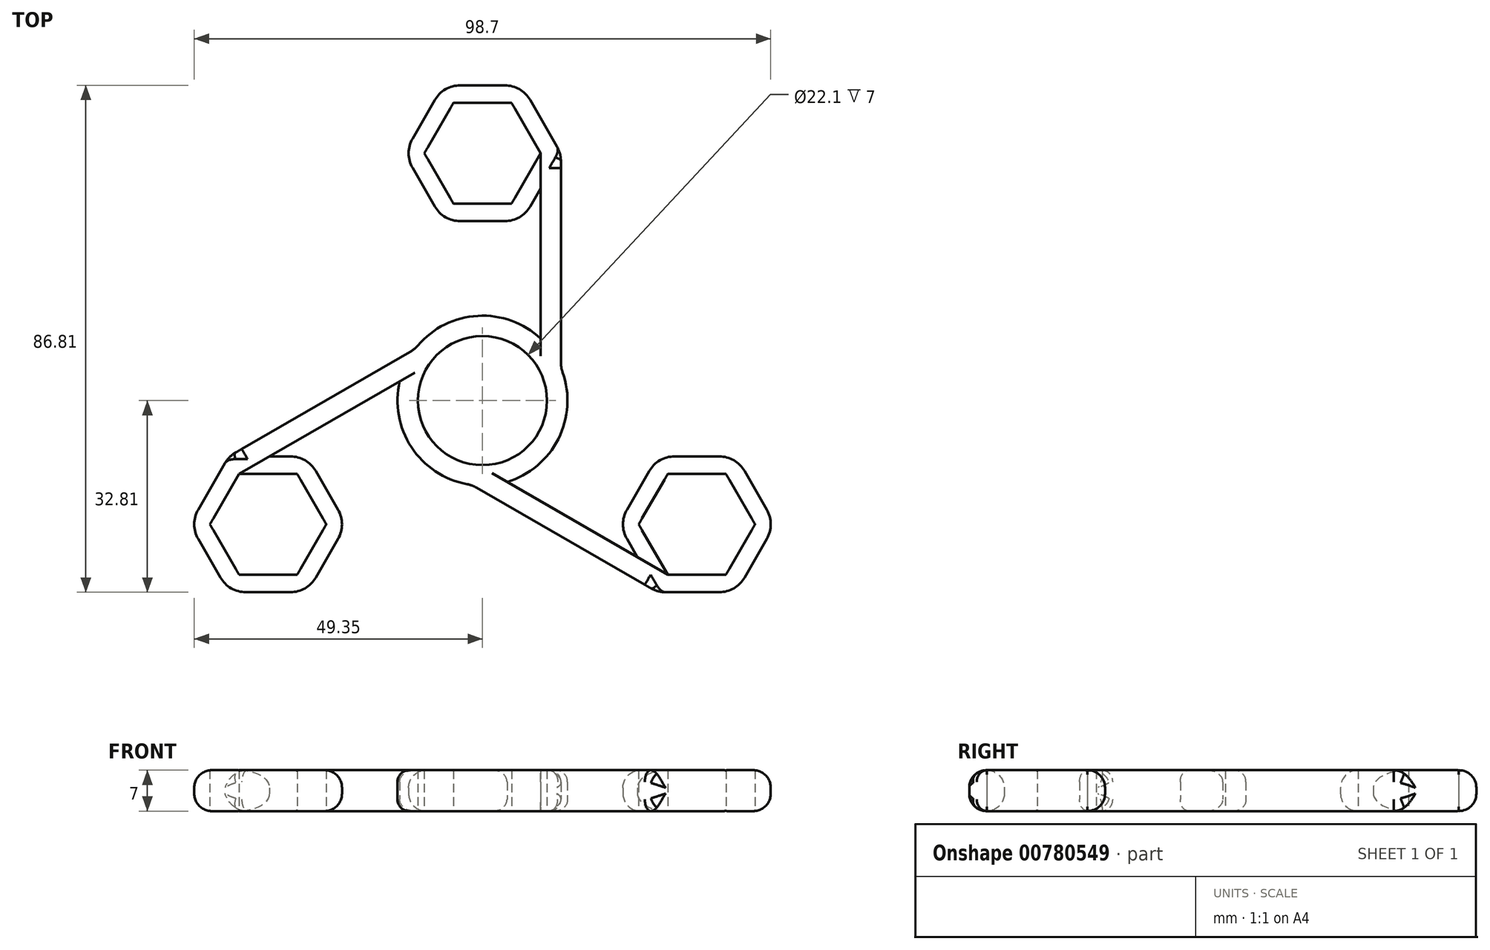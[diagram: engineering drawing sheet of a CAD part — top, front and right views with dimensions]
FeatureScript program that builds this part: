
annotation { "Feature Type Name" : "Feature", "Feature Type Description" : "" }
export const myFeature = defineFeature(function(context is Context, id is Id, definition is map)
    precondition{}
    {
        {
            var Q0;
            Q0=qCreatedBy(makeId("Top.planeOp"),FACE);
            var sketch = newSketch(context, id + "F0", { "sketchPlane" : qUnion([Q0])});
            skCircle(sketch, "E0", {"center": v(0, 0) * mm, "radius": 11.05 * mm});
            skCircle(sketch, "E1.0", {"center": v(0, 0) * mm, "radius": 14.55 * mm});
            skCircle(sketch, "E2.cCircle", {"center": v(0, 0) * mm, "radius": 19.75 * mm, "construction": true});
            skCircle(sketch, "E3.cCircle", {"center": v(0, 42.37) * mm, "radius": 8.62 * mm, "construction": true});
            skLineSegment(sketch, "E3.0", {"start": v(-4.98, 51) * mm, "end": v(4.98, 51) * mm});
            skLineSegment(sketch, "E3.1", {"start": v(4.98, 51) * mm, "end": v(9.96, 42.37) * mm});
            skLineSegment(sketch, "E3.2", {"start": v(9.96, 42.37) * mm, "end": v(4.98, 33.75) * mm});
            skLineSegment(sketch, "E3.3", {"start": v(4.98, 33.75) * mm, "end": v(-4.98, 33.75) * mm});
            skLineSegment(sketch, "E3.4", {"start": v(-4.98, 33.75) * mm, "end": v(-9.96, 42.37) * mm});
            skLineSegment(sketch, "E3.5", {"start": v(-9.96, 42.37) * mm, "end": v(-4.98, 51) * mm});
            skPoint(sketch, "E3.0.midPoint", {"position": v(0, 51) * mm});
            skLineSegment(sketch, "E4.0", {"start": v(-13.42, 42.37) * mm, "end": v(-6.71, 54) * mm});
            skLineSegment(sketch, "E4.1", {"start": v(6.71, 54) * mm, "end": v(13.42, 42.37) * mm});
            skLineSegment(sketch, "E4.2", {"start": v(13.42, 42.38) * mm, "end": v(6.71, 30.75) * mm});
            skLineSegment(sketch, "E4.3", {"start": v(-6.71, 54) * mm, "end": v(6.71, 54) * mm});
            skLineSegment(sketch, "E4.4", {"start": v(6.71, 30.75) * mm, "end": v(-6.71, 30.75) * mm});
            skLineSegment(sketch, "E4.5", {"start": v(-6.71, 30.75) * mm, "end": v(-13.42, 42.37) * mm});
            skLineSegment(sketch, "E5.bottom", {"start": v(9.96, 42.37) * mm, "end": v(13.42, 42.37) * mm});
            skLineSegment(sketch, "E5.top", {"start": v(9.96, 5.61) * mm, "end": v(13.42, 5.61) * mm});
            skLineSegment(sketch, "E5.left", {"start": v(9.96, 42.37) * mm, "end": v(9.96, 5.61) * mm});
            skLineSegment(sketch, "E5.right", {"start": v(13.42, 42.37) * mm, "end": v(13.42, 5.61) * mm});
            skSolve(sketch);
        }
        {
            var Q0;
            Q0=qSketchRegion(id+"F0",true);
            extrude(context, id + "F1", {"entities" : qUnion([Q0]), "depth" : 7 * mm, "offsetDistance" : 25 * mm});
        }
        {
            var Q0;
            Q0=makeQuery(id+"F1.opExtrude","SWEPT_EDGE",EDGE,{"disambiguationData":[OSD([sQuery(id+"F0.wireOp",EDGE,"e8ea1e39-c8e4-4f1f-8f41-e8bb20e3dc64.0"),sQuery(id+"F0.wireOp",EDGE,"e8ea1e39-c8e4-4f1f-8f41-e8bb20e3dc64.5")])]});
            var Q1;
            Q1=makeQuery(id+"F1.opExtrude","SWEPT_EDGE",EDGE,{"disambiguationData":[OSD([sQuery(id+"F0.wireOp",EDGE,"e8ea1e39-c8e4-4f1f-8f41-e8bb20e3dc64.2"),sQuery(id+"F0.wireOp",EDGE,"e8ea1e39-c8e4-4f1f-8f41-e8bb20e3dc64.4")])]});
            var Q2;
            Q2=makeQuery(id+"F1.opExtrude","SWEPT_EDGE",EDGE,{"disambiguationData":[OSD([sQuery(id+"F0.wireOp",EDGE,"e8ea1e39-c8e4-4f1f-8f41-e8bb20e3dc64.1"),sQuery(id+"F0.wireOp",EDGE,"e8ea1e39-c8e4-4f1f-8f41-e8bb20e3dc64.2")])]});
            var Q3;
            Q3=makeQuery(id+"F1.opExtrude","SWEPT_EDGE",EDGE,{"disambiguationData":[OSD([sQuery(id+"F0.wireOp",EDGE,"bc2e01c2-815f-4e23-ab08-36e09104f585.2"),sQuery(id+"F0.wireOp",EDGE,"bc2e01c2-815f-4e23-ab08-36e09104f585.4")])]});
            var Q4;
            Q4=makeQuery(id+"F1.opExtrude","SWEPT_EDGE",EDGE,{"disambiguationData":[OSD([sQuery(id+"F0.wireOp",EDGE,"bc2e01c2-815f-4e23-ab08-36e09104f585.1"),sQuery(id+"F0.wireOp",EDGE,"bc2e01c2-815f-4e23-ab08-36e09104f585.2")])]});
            var Q5;
            Q5=makeQuery(id+"F1.opExtrude","SWEPT_EDGE",EDGE,{"disambiguationData":[OSD([sQuery(id+"F0.wireOp",EDGE,"bc2e01c2-815f-4e23-ab08-36e09104f585.1"),sQuery(id+"F0.wireOp",EDGE,"bc2e01c2-815f-4e23-ab08-36e09104f585.3")])]});
            var Q6;
            Q6=makeQuery(id+"F1.opExtrude","SWEPT_EDGE",EDGE,{"disambiguationData":[OSD([sQuery(id+"F0.wireOp",EDGE,"bc2e01c2-815f-4e23-ab08-36e09104f585.0"),sQuery(id+"F0.wireOp",EDGE,"bc2e01c2-815f-4e23-ab08-36e09104f585.3")])]});
            var Q7;
            Q7=makeQuery(id+"F1.opExtrude","SWEPT_EDGE",EDGE,{"disambiguationData":[OSD([sQuery(id+"F0.wireOp",EDGE,"E4.1"),sQuery(id+"F0.wireOp",EDGE,"E4.2")])]});
            var Q8;
            Q8=makeQuery(id+"F1.opExtrude","SWEPT_EDGE",EDGE,{"disambiguationData":[OSD([sQuery(id+"F0.wireOp",EDGE,"E4.1"),sQuery(id+"F0.wireOp",EDGE,"E4.3")])]});
            var Q9;
            Q9=makeQuery(id+"F1.opExtrude","SWEPT_EDGE",EDGE,{"disambiguationData":[OSD([sQuery(id+"F0.wireOp",EDGE,"E4.0"),sQuery(id+"F0.wireOp",EDGE,"E4.3")])]});
            var Q10;
            Q10=makeQuery(id+"F1.opExtrude","SWEPT_EDGE",EDGE,{"disambiguationData":[OSD([sQuery(id+"F0.wireOp",EDGE,"E4.0"),sQuery(id+"F0.wireOp",EDGE,"E4.5")])]});
            var Q11;
            Q11=makeQuery(id+"F1.opExtrude","SWEPT_EDGE",EDGE,{"disambiguationData":[OSD([sQuery(id+"F0.wireOp",EDGE,"88b40c85-247c-4d13-ac2e-2eb34554f8ad.1"),sQuery(id+"F0.wireOp",EDGE,"88b40c85-247c-4d13-ac2e-2eb34554f8ad.3")])]});
            var Q12;
            Q12=makeQuery(id+"F1.opExtrude","SWEPT_EDGE",EDGE,{"disambiguationData":[OSD([sQuery(id+"F0.wireOp",EDGE,"88b40c85-247c-4d13-ac2e-2eb34554f8ad.0"),sQuery(id+"F0.wireOp",EDGE,"88b40c85-247c-4d13-ac2e-2eb34554f8ad.3")])]});
            var Q13;
            Q13=makeQuery(id+"F1.opExtrude","SWEPT_EDGE",EDGE,{"disambiguationData":[OSD([sQuery(id+"F0.wireOp",EDGE,"88b40c85-247c-4d13-ac2e-2eb34554f8ad.0"),sQuery(id+"F0.wireOp",EDGE,"88b40c85-247c-4d13-ac2e-2eb34554f8ad.5")])]});
            var Q14;
            Q14=makeQuery(id+"F1.opExtrude","SWEPT_EDGE",EDGE,{"disambiguationData":[OSD([sQuery(id+"F0.wireOp",EDGE,"88b40c85-247c-4d13-ac2e-2eb34554f8ad.4"),sQuery(id+"F0.wireOp",EDGE,"88b40c85-247c-4d13-ac2e-2eb34554f8ad.5")])]});
            var Q15;
            Q15=makeQuery(id+"F1.opExtrude","SWEPT_EDGE",EDGE,{"disambiguationData":[OSD([sQuery(id+"F0.wireOp",EDGE,"e039e999-560e-4138-92c9-75450f4679a6.0"),sQuery(id+"F0.wireOp",EDGE,"e039e999-560e-4138-92c9-75450f4679a6.3")])]});
            var Q16;
            Q16=makeQuery(id+"F1.opExtrude","SWEPT_EDGE",EDGE,{"disambiguationData":[OSD([sQuery(id+"F0.wireOp",EDGE,"e039e999-560e-4138-92c9-75450f4679a6.0"),sQuery(id+"F0.wireOp",EDGE,"e039e999-560e-4138-92c9-75450f4679a6.5")])]});
            var Q17;
            Q17=makeQuery(id+"F1.opExtrude","SWEPT_EDGE",EDGE,{"disambiguationData":[OSD([sQuery(id+"F0.wireOp",EDGE,"e039e999-560e-4138-92c9-75450f4679a6.4"),sQuery(id+"F0.wireOp",EDGE,"e039e999-560e-4138-92c9-75450f4679a6.5")])]});
            var Q18;
            Q18=makeQuery(id+"F1.opExtrude","SWEPT_EDGE",EDGE,{"disambiguationData":[OSD([sQuery(id+"F0.wireOp",EDGE,"e039e999-560e-4138-92c9-75450f4679a6.2"),sQuery(id+"F0.wireOp",EDGE,"e039e999-560e-4138-92c9-75450f4679a6.4")])]});
            var Q19;
            Q19=makeQuery(id+"F1.opExtrude","SWEPT_EDGE",EDGE,{"disambiguationData":[OSD([sQuery(id+"F0.wireOp",EDGE,"e8ea1e39-c8e4-4f1f-8f41-e8bb20e3dc64.4"),sQuery(id+"F0.wireOp",EDGE,"e8ea1e39-c8e4-4f1f-8f41-e8bb20e3dc64.5")])]});
            var Q20;
            Q20=makeQuery(id+"F1.opExtrude","SWEPT_EDGE",EDGE,{"disambiguationData":[OSD([sQuery(id+"F0.wireOp",EDGE,"E4.4"),sQuery(id+"F0.wireOp",EDGE,"E4.5")])]});
            var Q21;
            Q21=makeQuery(id+"F1.opExtrude","SWEPT_EDGE",EDGE,{"disambiguationData":[OSD([sQuery(id+"F0.wireOp",EDGE,"E4.2"),sQuery(id+"F0.wireOp",EDGE,"E4.4")])]});
            var Q22;
            Q22=makeQuery(id+"F1.opExtrude","SWEPT_EDGE",EDGE,{"disambiguationData":[OSD([sQuery(id+"F0.wireOp",EDGE,"E1.0"),sQuery(id+"F0.wireOp",EDGE,"E5.top"),sQuery(id+"F0.wireOp",EDGE,"E5.right")])]});
            fillet(context, id + "F2", {"entities" : qUnion([Q0, Q1, Q2, Q3, Q4, Q5, Q6, Q7, Q8, Q9, Q10, Q11, Q12, Q13, Q14, Q15, Q16, Q17, Q18, Q19, Q20, Q21, Q22]), "radius" : 5 * mm, "tangentPropagation" : true, "allowEdgeOverflow" : false});
        }
        {
            var Q0;
            Q0=makeQuery(id+"F1.opExtrude","CAP_EDGE",EDGE,{"disambiguationData":[OSD([sQuery(id+"F0.wireOp",EDGE,"e039e999-560e-4138-92c9-75450f4679a6.4")])],"isStart":true});
            var Q1;
            Q1=makeQuery(id+"F1.opExtrude","CAP_EDGE",EDGE,{"disambiguationData":[OSD([sQuery(id+"F0.wireOp",EDGE,"e8ea1e39-c8e4-4f1f-8f41-e8bb20e3dc64.5")])],"isStart":true});
            var Q2;
            Q2=makeQuery(id+"F1.opExtrude","CAP_EDGE",EDGE,{"disambiguationData":[OSD([sQuery(id+"F0.wireOp",EDGE,"bc2e01c2-815f-4e23-ab08-36e09104f585.2")])],"isStart":true});
            var Q3;
            Q3=makeQuery(id+"F1.opExtrude","CAP_EDGE",EDGE,{"disambiguationData":[OSD([sQuery(id+"F0.wireOp",EDGE,"E4.2")])],"isStart":true});
            var Q4;
            Q4=makeQuery(id+"F1.opExtrude","CAP_EDGE",EDGE,{"disambiguationData":[OSD([sQuery(id+"F0.wireOp",EDGE,"88b40c85-247c-4d13-ac2e-2eb34554f8ad.3")])],"isStart":true});
            var Q5;
            Q5=makeQuery(id+"F1.opExtrude","CAP_EDGE",EDGE,{"disambiguationData":[OSD([sQuery(id+"F0.wireOp",EDGE,"bc2e01c2-815f-4e23-ab08-36e09104f585.1")])],"isStart":false});
            var Q6;
            Q6=makeQuery(id+"F1.opExtrude","CAP_EDGE",EDGE,{"disambiguationData":[OSD([sQuery(id+"F0.wireOp",EDGE,"e8ea1e39-c8e4-4f1f-8f41-e8bb20e3dc64.2")])],"isStart":false});
            var Q7;
            Q7=makeQuery(id+"F1.opExtrude","CAP_EDGE",EDGE,{"disambiguationData":[OSD([sQuery(id+"F0.wireOp",EDGE,"e039e999-560e-4138-92c9-75450f4679a6.5")])],"isStart":false});
            var Q8;
            Q8=makeQuery(id+"F1.opExtrude","CAP_EDGE",EDGE,{"disambiguationData":[OSD([sQuery(id+"F0.wireOp",EDGE,"88b40c85-247c-4d13-ac2e-2eb34554f8ad.5")])],"isStart":false});
            var Q9;
            Q9=makeQuery(id+"F1.opExtrude","CAP_EDGE",EDGE,{"disambiguationData":[OSD([sQuery(id+"F0.wireOp",EDGE,"E4.0")])],"isStart":false});
            var Q10;
            Q10=makeQuery(id+"F1.opExtrude","CAP_EDGE",EDGE,{"disambiguationData":[OSD([sQuery(id+"F0.wireOp",EDGE,"E4.1")])],"isStart":false});
            var Q11;
            Q11=makeQuery(id+"F1.opExtrude","CAP_EDGE",EDGE,{"disambiguationData":[OSD([sQuery(id+"F0.wireOp",EDGE,"E4.1")])],"isStart":true});
            var Q12;
            Q12=makeQuery(id+"F1.opExtrude","CAP_EDGE",EDGE,{"disambiguationData":[OSD([sQuery(id+"F0.wireOp",EDGE,"E4.2")])],"isStart":false});
            var Q13;
            Q13=makeQuery(id+"F1.opExtrude","CAP_EDGE",EDGE,{"disambiguationData":[OSD([sQuery(id+"F0.wireOp",EDGE,"E4.4")])],"isStart":false});
            var Q14;
            Q14=makeQuery(id+"F1.opExtrude","CAP_EDGE",EDGE,{"disambiguationData":[OSD([sQuery(id+"F0.wireOp",EDGE,"E4.5")])],"isStart":false});
            var Q15;
            Q15=makeQuery(id+"F1.opExtrude","CAP_EDGE",EDGE,{"disambiguationData":[OSD([sQuery(id+"F0.wireOp",EDGE,"E4.4")])],"isStart":true});
            var Q16;
            Q16=makeQuery(id+"F1.opExtrude","CAP_EDGE",EDGE,{"disambiguationData":[OSD([sQuery(id+"F0.wireOp",EDGE,"E4.5")])],"isStart":true});
            var Q17;
            Q17=makeQuery(id+"F1.opExtrude","CAP_EDGE",EDGE,{"disambiguationData":[OSD([sQuery(id+"F0.wireOp",EDGE,"E4.0")])],"isStart":true});
            var Q18;
            Q18=makeQuery(id+"F1.opExtrude","CAP_EDGE",EDGE,{"disambiguationData":[OSD([sQuery(id+"F0.wireOp",EDGE,"E4.3")])],"isStart":true});
            var Q19;
            Q19=makeQuery(id+"F1.opExtrude","CAP_EDGE",EDGE,{"disambiguationData":[OSD([sQuery(id+"F0.wireOp",EDGE,"E4.3")])],"isStart":false});
            fillet(context, id + "F3", {"entities" : qUnion([Q0, Q1, Q2, Q3, Q4, Q5, Q6, Q7, Q8, Q9, Q10, Q11, Q12, Q13, Q14, Q15, Q16, Q17, Q18, Q19]), "radius" : 3 * mm, "allowEdgeOverflow" : false});
        }
        {
            var Q0;
            {var subQ0=sQuery(id+"F0.wireOp",EDGE,"E1.0");Q0=makeQuery(id+"F1.opExtrude","CAP_EDGE",EDGE,{"disambiguationData":[OSD([subQ0]),TDD([makeQuery(id+"F0.imprint","IMPRINT",EDGE,{"disambiguationData":[TD([[makeQuery(id+"F0.imprint","INTERSECT",VERTEX,{"derivedFrom":[subQ0,sQuery(id+"F0.wireOp",EDGE,"e039e999-560e-4138-92c9-75450f4679a6.2")]}),-1.0]])],"derivedFrom":subQ0})])],"isStart":false});}
            var Q1;
            {var subQ0=sQuery(id+"F0.wireOp",EDGE,"E1.0");Q1=makeQuery(id+"F1.opExtrude","CAP_EDGE",EDGE,{"disambiguationData":[OSD([subQ0]),TDD([makeQuery(id+"F0.imprint","IMPRINT",EDGE,{"disambiguationData":[TD([[makeQuery(id+"F0.imprint","INTERSECT",VERTEX,{"derivedFrom":[subQ0,sQuery(id+"F0.wireOp",EDGE,"e8ea1e39-c8e4-4f1f-8f41-e8bb20e3dc64.1")]}),-1.0]])],"derivedFrom":subQ0})])],"isStart":false});}
            var Q2;
            {var subQ0=sQuery(id+"F0.wireOp",EDGE,"E1.0");Q2=makeQuery(id+"F1.opExtrude","CAP_EDGE",EDGE,{"disambiguationData":[OSD([subQ0]),TDD([makeQuery(id+"F0.imprint","IMPRINT",EDGE,{"disambiguationData":[TD([[makeQuery(id+"F0.imprint","INTERSECT",VERTEX,{"derivedFrom":[subQ0,sQuery(id+"F0.wireOp",EDGE,"E4.2")]}),1.0]])],"derivedFrom":subQ0})])],"isStart":false});}
            var Q3;
            {var subQ0=sQuery(id+"F0.wireOp",EDGE,"E1.0");Q3=makeQuery(id+"F1.opExtrude","CAP_EDGE",EDGE,{"disambiguationData":[OSD([subQ0]),TDD([makeQuery(id+"F0.imprint","IMPRINT",EDGE,{"disambiguationData":[TD([[makeQuery(id+"F0.imprint","INTERSECT",VERTEX,{"derivedFrom":[subQ0,sQuery(id+"F0.wireOp",EDGE,"E4.5")]}),-1.0]])],"derivedFrom":subQ0})])],"isStart":false});}
            var Q4;
            {var subQ0=sQuery(id+"F0.wireOp",EDGE,"E1.0");Q4=makeQuery(id+"F1.opExtrude","CAP_EDGE",EDGE,{"disambiguationData":[OSD([subQ0]),TDD([makeQuery(id+"F0.imprint","IMPRINT",EDGE,{"disambiguationData":[TD([[makeQuery(id+"F0.imprint","INTERSECT",VERTEX,{"derivedFrom":[subQ0,sQuery(id+"F0.wireOp",EDGE,"88b40c85-247c-4d13-ac2e-2eb34554f8ad.4")]}),-1.0]])],"derivedFrom":subQ0})])],"isStart":false});}
            var Q5;
            {var subQ0=sQuery(id+"F0.wireOp",EDGE,"E1.0");Q5=makeQuery(id+"F1.opExtrude","CAP_EDGE",EDGE,{"disambiguationData":[OSD([subQ0]),TDD([makeQuery(id+"F0.imprint","IMPRINT",EDGE,{"disambiguationData":[TD([[makeQuery(id+"F0.imprint","INTERSECT",VERTEX,{"derivedFrom":[subQ0,sQuery(id+"F0.wireOp",EDGE,"e039e999-560e-4138-92c9-75450f4679a6.2")]}),-1.0]])],"derivedFrom":subQ0})])],"isStart":true});}
            var Q6;
            {var subQ0=sQuery(id+"F0.wireOp",EDGE,"E1.0");Q6=makeQuery(id+"F1.opExtrude","CAP_EDGE",EDGE,{"disambiguationData":[OSD([subQ0]),TDD([makeQuery(id+"F0.imprint","IMPRINT",EDGE,{"disambiguationData":[TD([[makeQuery(id+"F0.imprint","INTERSECT",VERTEX,{"derivedFrom":[subQ0,sQuery(id+"F0.wireOp",EDGE,"e8ea1e39-c8e4-4f1f-8f41-e8bb20e3dc64.1")]}),-1.0]])],"derivedFrom":subQ0})])],"isStart":true});}
            var Q7;
            {var subQ0=sQuery(id+"F0.wireOp",EDGE,"E1.0");Q7=makeQuery(id+"F1.opExtrude","CAP_EDGE",EDGE,{"disambiguationData":[OSD([subQ0]),TDD([makeQuery(id+"F0.imprint","IMPRINT",EDGE,{"disambiguationData":[TD([[makeQuery(id+"F0.imprint","INTERSECT",VERTEX,{"derivedFrom":[subQ0,sQuery(id+"F0.wireOp",EDGE,"E4.2")]}),1.0]])],"derivedFrom":subQ0})])],"isStart":true});}
            var Q8;
            {var subQ0=sQuery(id+"F0.wireOp",EDGE,"E1.0");Q8=makeQuery(id+"F1.opExtrude","CAP_EDGE",EDGE,{"disambiguationData":[OSD([subQ0]),TDD([makeQuery(id+"F0.imprint","IMPRINT",EDGE,{"disambiguationData":[TD([[makeQuery(id+"F0.imprint","INTERSECT",VERTEX,{"derivedFrom":[subQ0,sQuery(id+"F0.wireOp",EDGE,"E4.5")]}),-1.0]])],"derivedFrom":subQ0})])],"isStart":true});}
            var Q9;
            {var subQ0=sQuery(id+"F0.wireOp",EDGE,"E1.0");Q9=makeQuery(id+"F1.opExtrude","CAP_EDGE",EDGE,{"disambiguationData":[OSD([subQ0]),TDD([makeQuery(id+"F0.imprint","IMPRINT",EDGE,{"disambiguationData":[TD([[makeQuery(id+"F0.imprint","INTERSECT",VERTEX,{"derivedFrom":[subQ0,sQuery(id+"F0.wireOp",EDGE,"88b40c85-247c-4d13-ac2e-2eb34554f8ad.4")]}),-1.0]])],"derivedFrom":subQ0})])],"isStart":true});}
            fillet(context, id + "F4", {"entities" : qUnion([Q0, Q1, Q2, Q3, Q4, Q5, Q6, Q7, Q8, Q9]), "radius" : 2 * mm, "tangentPropagation" : true, "allowEdgeOverflow" : false});
        }
        {
            var Q0;
            Q0=makeQuery(id+"F1.opExtrude","SWEPT_BODY",BODY,{"disambiguationData":[OSD([sQuery(id+"F0.wireOp",EDGE,"E0"),sQuery(id+"F0.wireOp",EDGE,"E1.0"),sQuery(id+"F0.wireOp",EDGE,"E3.0"),sQuery(id+"F0.wireOp",EDGE,"E3.1"),sQuery(id+"F0.wireOp",EDGE,"E3.2"),sQuery(id+"F0.wireOp",EDGE,"E3.3"),sQuery(id+"F0.wireOp",EDGE,"E3.4"),sQuery(id+"F0.wireOp",EDGE,"E3.5"),sQuery(id+"F0.wireOp",EDGE,"E4.0"),sQuery(id+"F0.wireOp",EDGE,"E4.1"),sQuery(id+"F0.wireOp",EDGE,"E4.2"),sQuery(id+"F0.wireOp",EDGE,"E4.3"),sQuery(id+"F0.wireOp",EDGE,"E4.5")])]});
            var Q1;
            Q1=makeQuery(id+"F1.opExtrude","SWEPT_FACE",FACE,{"disambiguationData":[OSD([sQuery(id+"F0.wireOp",EDGE,"E0")])]});
            circularPattern(context, id + "F5", {"operationType" : NewBodyOperationType.ADD, "entities" : qUnion([Q0]), "axis" : qUnion([Q1]), "angle" : 360 * degree, "instanceCount" : 3, "equalSpace" : true});
        }
    });
